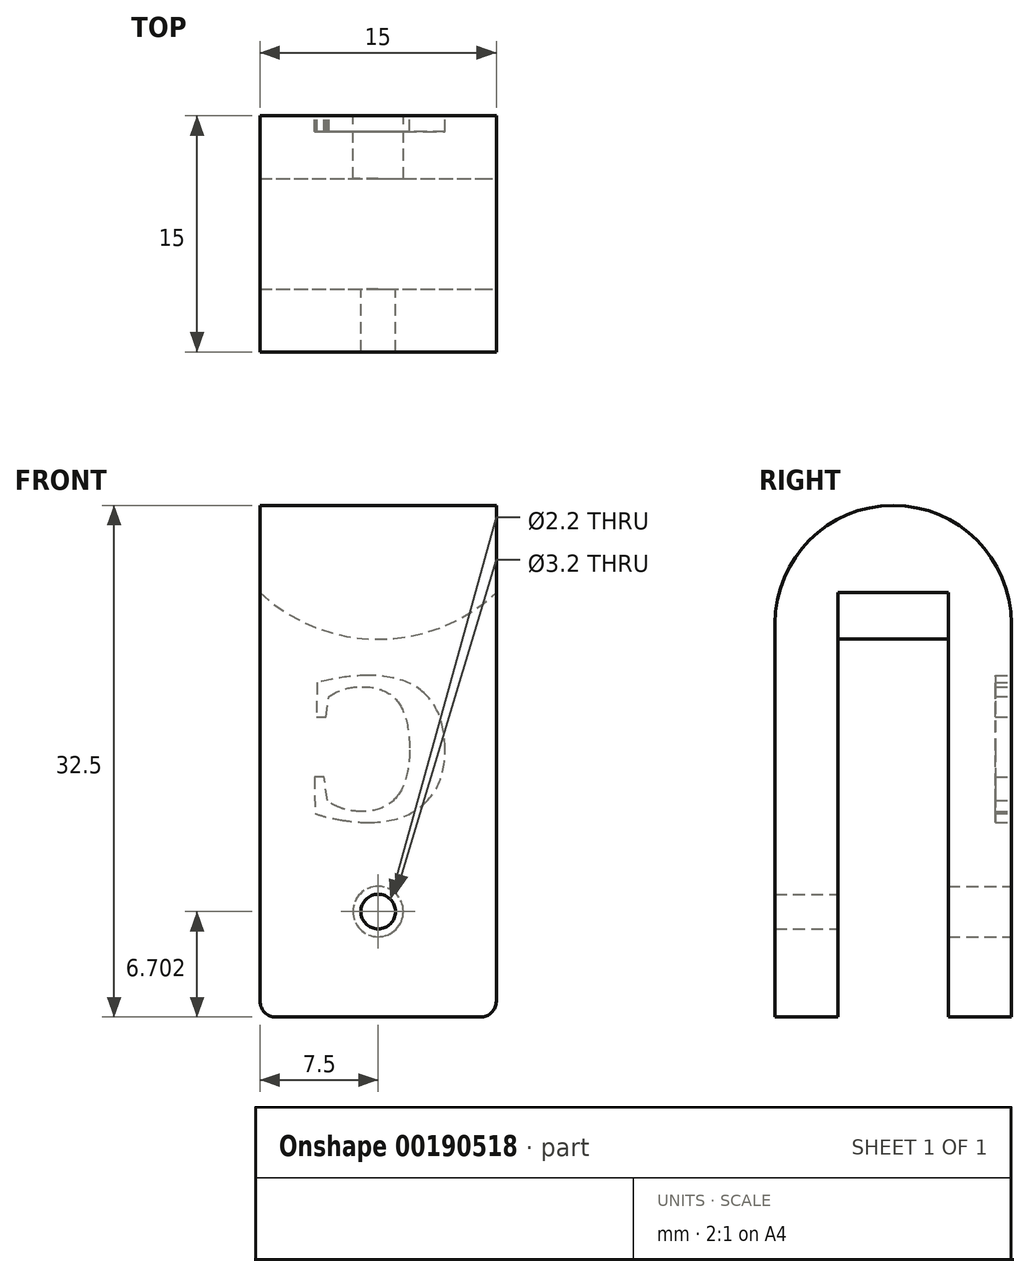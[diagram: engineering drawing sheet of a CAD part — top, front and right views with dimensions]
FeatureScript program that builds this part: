
annotation { "Feature Type Name" : "Feature", "Feature Type Description" : "" }
export const myFeature = defineFeature(function(context is Context, id is Id, definition is map)
    precondition{}
    {
        {
            var Q0;
            Q0=qCreatedBy(makeId("Right.planeOp"),FACE);
            var sketch = newSketch(context, id + "F0", { "sketchPlane" : qUnion([Q0])});
            skArc(sketch, "E0", {"start": v(7.5, 0) * mm, "mid": v(0, 7.5) * mm, "end": v(-7.5, 0) * mm});
            skLineSegment(sketch, "E1.top", {"start": v(-7.5, -25) * mm, "end": v(7.5, -25) * mm});
            skLineSegment(sketch, "E1.left", {"start": v(-7.5, 0) * mm, "end": v(-7.5, -25) * mm});
            skLineSegment(sketch, "E1.right", {"start": v(7.5, 0) * mm, "end": v(7.5, -25) * mm});
            skSolve(sketch);
        }
        {
            var Q0;
            Q0=makeQuery(id+"F0.imprint","IMPRINT",FACE,{"disambiguationData":[TD([[makeQuery(id+"F0.imprint","IMPRINT",EDGE,{"derivedFrom":sQuery(id+"F0.wireOp",EDGE,"E0")}),1.0]])]});
            extrude(context, id + "F1", {"entities" : qUnion([Q0]), "depth" : 15 * mm});
        }
        {
            var Q0;
            Q0=qCreatedBy(makeId("Front.planeOp"),FACE);
            var sketch = newSketch(context, id + "F2", { "sketchPlane" : qUnion([Q0])});
            skLineSegment(sketch, "E2", {"start": v(7.5, 15) * mm, "end": v(7.5, -25.74) * mm, "construction": true});
            skLineSegment(sketch, "E3.top", {"start": v(15.43, -31.52) * mm, "end": v(-0.4, -31.52) * mm});
            skLineSegment(sketch, "E3.left", {"start": v(15.43, 2.38) * mm, "end": v(15.43, -31.52) * mm});
            skLineSegment(sketch, "E3.right", {"start": v(-0.4, 2.39) * mm, "end": v(-0.4, -31.52) * mm});
            skArc(sketch, "E4.converted", {"start": v(-0.4, 2.35) * mm, "mid": v(7.52, -1) * mm, "end": v(15.43, 2.38) * mm});
            skSolve(sketch);
        }
        {
            var Q0;
            {var subQ0=sQuery(id+"F2.wireOp",EDGE,"E3.top");Q0=makeQuery(id+"F2.imprint","IMPRINT",FACE,{"disambiguationData":[TD([[makeQuery(id+"F2.imprint","IMPRINT",EDGE,{"derivedFrom":subQ0}),-1.0]])]});}
            extrude(context, id + "F3", {"entities" : qUnion([Q0]), "operationType" : NewBodyOperationType.REMOVE, "endBound" : BoundingType.SYMMETRIC, "oppositeDirection" : true, "depth" : 7 * mm});
        }
        {
            var Q0;
            Q0=makeQuery(id+"F1.opExtrude","SWEPT_FACE",FACE,{"disambiguationData":[OSD([sQuery(id+"F0.wireOp",EDGE,"E1.right")])]});
            var sketch = newSketch(context, id + "F4", { "sketchPlane" : qUnion([Q0])});
            skLineSegment(sketch, "E5", {"start": v(-7.5, -25) * mm, "end": v(-7.5, -3.98) * mm, "construction": true});
            skCircle(sketch, "E6", {"center": v(-7.5, -18.3) * mm, "radius": 1.1 * mm});
            skSolve(sketch);
        }
        {
            var Q0;
            Q0=makeQuery(id+"F4.imprint","IMPRINT",FACE,{"disambiguationData":[TD([[makeQuery(id+"F4.imprint","IMPRINT",EDGE,{"derivedFrom":sQuery(id+"F4.wireOp",EDGE,"E6")}),1.0]])]});
            extrude(context, id + "F5", {"entities" : qUnion([Q0]), "operationType" : NewBodyOperationType.REMOVE, "endBound" : BoundingType.THROUGH_ALL, "oppositeDirection" : true, "depth" : 25 * mm});
        }
        {
            var Q0;
            {var subQ0=sQuery(id+"F0.wireOp",EDGE,"E1.right");var subQ1=sQuery(id+"F0.wireOp",EDGE,"E1.top");Q0=makeQuery(id+"F3.boolean.opBoolean","SPLIT",EDGE,{"disambiguationData":[TD([makeQuery(id+"F1.opExtrude","SWEPT_FACE",FACE,{"disambiguationData":[OSD([subQ0])]})])],"derivedFrom":makeQuery(id+"F1.opExtrude","CAP_EDGE",EDGE,{"disambiguationData":[OSD([subQ1])],"isStart":false})});}
            var Q1;
            {var subQ0=sQuery(id+"F0.wireOp",EDGE,"E1.left");var subQ1=sQuery(id+"F0.wireOp",EDGE,"E1.top");Q1=makeQuery(id+"F3.boolean.opBoolean","SPLIT",EDGE,{"disambiguationData":[TD([makeQuery(id+"F1.opExtrude","SWEPT_FACE",FACE,{"disambiguationData":[OSD([subQ0])]})])],"derivedFrom":makeQuery(id+"F1.opExtrude","CAP_EDGE",EDGE,{"disambiguationData":[OSD([subQ1])],"isStart":false})});}
            var Q2;
            {var subQ0=sQuery(id+"F0.wireOp",EDGE,"E1.right");var subQ1=sQuery(id+"F0.wireOp",EDGE,"E1.top");Q2=makeQuery(id+"F3.boolean.opBoolean","SPLIT",EDGE,{"disambiguationData":[TD([makeQuery(id+"F1.opExtrude","SWEPT_FACE",FACE,{"disambiguationData":[OSD([subQ0])]})])],"derivedFrom":makeQuery(id+"F1.opExtrude","CAP_EDGE",EDGE,{"disambiguationData":[OSD([subQ1])],"isStart":true})});}
            var Q3;
            {var subQ0=sQuery(id+"F0.wireOp",EDGE,"E1.left");var subQ1=sQuery(id+"F0.wireOp",EDGE,"E1.top");Q3=makeQuery(id+"F3.boolean.opBoolean","SPLIT",EDGE,{"disambiguationData":[TD([makeQuery(id+"F1.opExtrude","SWEPT_FACE",FACE,{"disambiguationData":[OSD([subQ0])]})])],"derivedFrom":makeQuery(id+"F1.opExtrude","CAP_EDGE",EDGE,{"disambiguationData":[OSD([subQ1])],"isStart":true})});}
            fillet(context, id + "F6", {"entities" : qUnion([Q0, Q1, Q2, Q3]), "radius" : 1 * mm, "tangentPropagation" : true, "allowEdgeOverflow" : false});
        }
        {
            var Q0;
            Q0=makeQuery(id+"F1.opExtrude","SWEPT_FACE",FACE,{"disambiguationData":[OSD([sQuery(id+"F0.wireOp",EDGE,"E1.right")])]});
            var sketch = newSketch(context, id + "F7", { "sketchPlane" : qUnion([Q0])});
            skText(sketch, "E7", { "text": "C", "fontName": "Tinos-Bold.ttf"});
            const initialGuessF7  = {"E7": [-0.01242, -0.0125, 1, 0, 0.01]};
            skSetInitialGuess(sketch, initialGuessF7);
            skSolve(sketch);
        }
        {
            var Q0;
            Q0 = qSketchRegion(id + "F7", true);
            extrude(context, id + "F8", {"entities" : qUnion([Q0]), "operationType" : NewBodyOperationType.REMOVE, "oppositeDirection" : true, "depth" : 1 * mm});
        }
        {
            var Q0;
            Q0=makeQuery(id+"F1.opExtrude","SWEPT_FACE",FACE,{"disambiguationData":[OSD([sQuery(id+"F0.wireOp",EDGE,"E1.right")])]});
            var sketch = newSketch(context, id + "F9", { "sketchPlane" : qUnion([Q0])});
            skCircle(sketch, "E8", {"center": v(-7.5, -18.3) * mm, "radius": 1.6 * mm});
            skSolve(sketch);
        }
        {
            var Q0;
            Q0=makeQuery(id+"F9.imprint","IMPRINT",FACE,{"disambiguationData":[TD([[makeQuery(id+"F9.imprint","IMPRINT",EDGE,{"derivedFrom":sQuery(id+"F9.wireOp",EDGE,"E8")}),1.0]])]});
            extrude(context, id + "F10", {"entities" : qUnion([Q0]), "operationType" : NewBodyOperationType.REMOVE, "oppositeDirection" : true, "depth" : 5 * mm});
        }
    });
